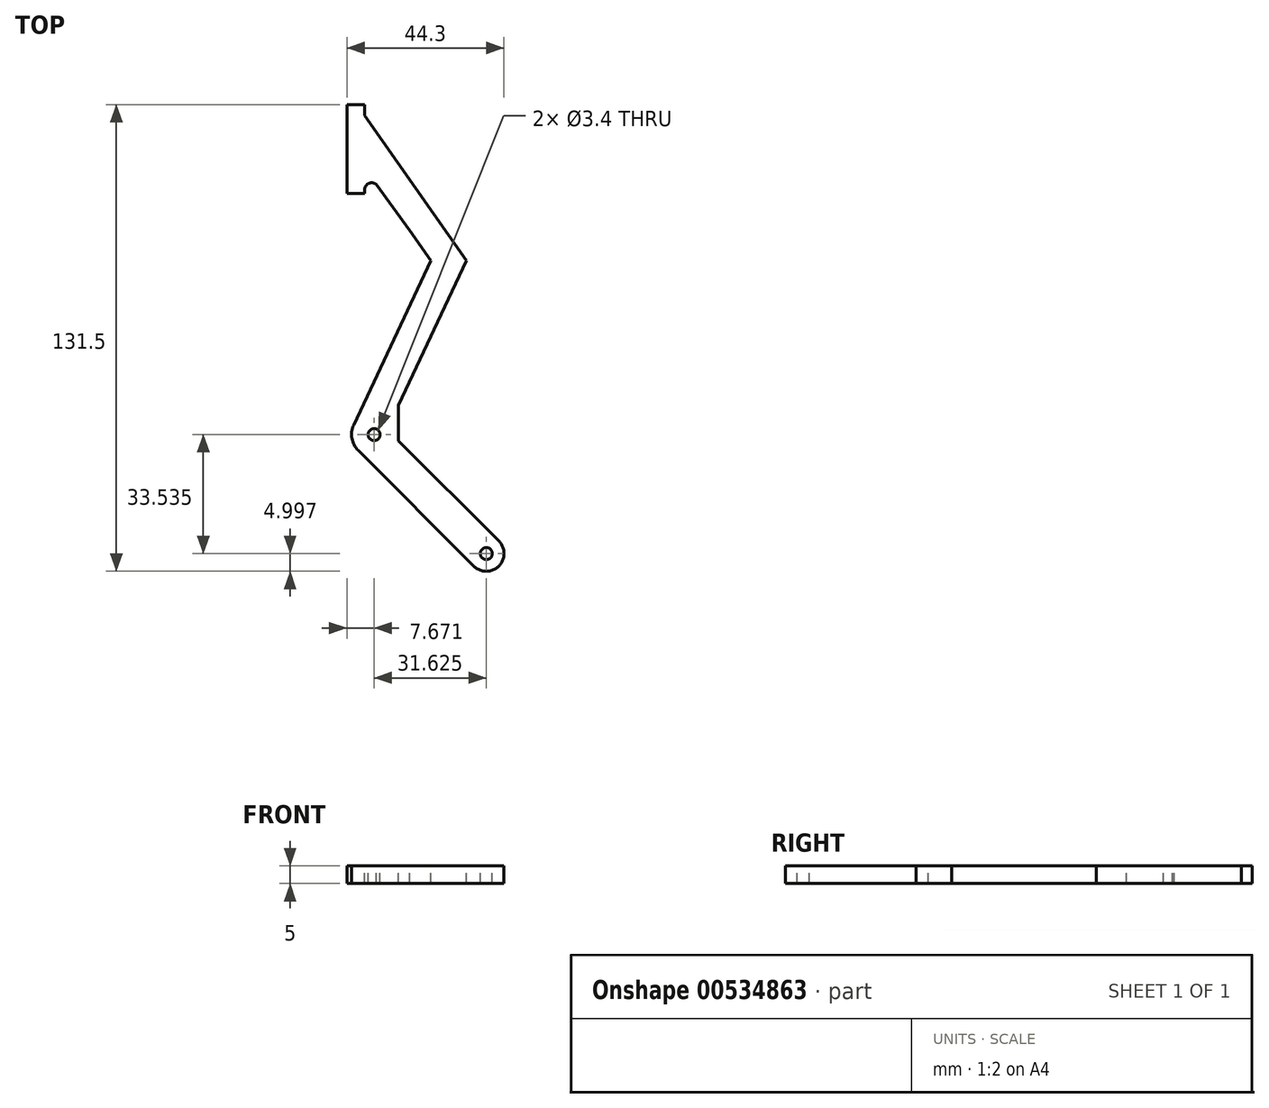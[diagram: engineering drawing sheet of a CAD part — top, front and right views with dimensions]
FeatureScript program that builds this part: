
annotation { "Feature Type Name" : "Feature", "Feature Type Description" : "" }
export const myFeature = defineFeature(function(context is Context, id is Id, definition is map)
    precondition{}
    {
        {
            var Q0;
            Q0=qCreatedBy(makeId("Top.planeOp"),FACE);
            var sketch = newSketch(context, id + "F0", { "sketchPlane" : qUnion([Q0])});
            skLineSegment(sketch, "E0", {"start": v(9.55, 67.67) * mm, "end": v(14.55, 67.67) * mm});
            skLineSegment(sketch, "E1", {"start": v(14.55, 67.67) * mm, "end": v(14.55, 42.67) * mm});
            skLineSegment(sketch, "E2", {"start": v(14.55, 42.67) * mm, "end": v(9.55, 42.67) * mm});
            skLineSegment(sketch, "E3", {"start": v(9.55, 67.67) * mm, "end": v(9.55, 64.67) * mm});
            skLineSegment(sketch, "E4", {"start": v(9.55, 42.67) * mm, "end": v(9.55, 43.67) * mm});
            skLineSegment(sketch, "E5", {"start": v(9.55, 64.67) * mm, "end": v(-19.12, 23.72) * mm});
            skLineSegment(sketch, "E6", {"start": v(-19.12, 23.72) * mm, "end": v(0.01, -17.01) * mm});
            skLineSegment(sketch, "E7", {"start": v(-9.12, 23.72) * mm, "end": v(12.63, -22.6) * mm});
            skLineSegment(sketch, "E8", {"start": v(0.01, -17.01) * mm, "end": v(0.01, -27.01) * mm});
            skLineSegment(sketch, "E9", {"start": v(0.01, -27.01) * mm, "end": v(-28.27, -55.3) * mm});
            skLineSegment(sketch, "E10", {"start": v(-9.12, 23.72) * mm, "end": v(-3.12, 32.3) * mm});
            skArc(sketch, "E11", {"start": v(9.55, 43.67) * mm, "mid": v(8.39, 45.5) * mm, "end": v(6.24, 45.19) * mm});
            skLineSegment(sketch, "E12", {"start": v(-3.12, 32.3) * mm, "end": v(6.24, 45.19) * mm});
            skLineSegment(sketch, "E13", {"start": v(0.01, -27.01) * mm, "end": v(7.08, -34.08) * mm});
            skLineSegment(sketch, "E14", {"start": v(7.08, -34.08) * mm, "end": v(11.38, -29.79) * mm});
            skPoint(sketch, "E15.newPointA", {"position": v(16.39, -30.59) * mm});
            skArc(sketch, "E15.filletArc", {"start": v(11.38, -29.79) * mm, "mid": v(13.14, -26.4) * mm, "end": v(12.63, -22.6) * mm});
            skCircle(sketch, "E16", {"center": v(6.89, -25.3) * mm, "radius": 1.7 * mm});
            skLineSegment(sketch, "E17", {"start": v(7.08, -34.08) * mm, "end": v(-21.2, -62.37) * mm});
            skLineSegment(sketch, "E18", {"start": v(-21.2, -62.37) * mm, "end": v(-28.27, -55.3) * mm});
            skArc(sketch, "E19", {"start": v(-28.27, -55.3) * mm, "mid": v(-28.27, -62.37) * mm, "end": v(-21.2, -62.37) * mm});
            skCircle(sketch, "E20", {"center": v(-24.74, -58.83) * mm, "radius": 1.7 * mm});
            skSolve(sketch);
        }
        {
            var Q0;
            Q0=qSketchRegion(id+"F0",true);
            extrude(context, id + "F1", {"entities" : qUnion([Q0]), "depth" : 5 * mm});
        }
        {
            var Q0;
            Q0=makeQuery(id+"F1.opExtrude","SWEPT_BODY",BODY,{"disambiguationData":[OSD([sQuery(id+"F0.wireOp",EDGE,"E0"),sQuery(id+"F0.wireOp",EDGE,"E1"),sQuery(id+"F0.wireOp",EDGE,"E2"),sQuery(id+"F0.wireOp",EDGE,"E3"),sQuery(id+"F0.wireOp",EDGE,"E4"),sQuery(id+"F0.wireOp",EDGE,"E5"),sQuery(id+"F0.wireOp",EDGE,"E6"),sQuery(id+"F0.wireOp",EDGE,"E7"),sQuery(id+"F0.wireOp",EDGE,"E8"),sQuery(id+"F0.wireOp",EDGE,"E9"),sQuery(id+"F0.wireOp",EDGE,"E10"),sQuery(id+"F0.wireOp",EDGE,"E11"),sQuery(id+"F0.wireOp",EDGE,"E12"),sQuery(id+"F0.wireOp",EDGE,"E14"),sQuery(id+"F0.wireOp",EDGE,"E15.filletArc"),sQuery(id+"F0.wireOp",EDGE,"E16"),sQuery(id+"F0.wireOp",EDGE,"E17"),sQuery(id+"F0.wireOp",EDGE,"E19"),sQuery(id+"F0.wireOp",EDGE,"E20")])]});
            var Q1;
            Q1=makeQuery(id+"F1.opExtrude","CAP_EDGE",EDGE,{"disambiguationData":[OSD([sQuery(id+"F0.wireOp",EDGE,"E1")])],"isStart":false});
            transform(context, id + "F2", {"entities" : qUnion([Q0]), "transformType" : TransformType.ROTATION, "transformAxis" : qUnion([Q1]), "angle" : 180 * degree, "makeCopy" : false});
        }
        {
            var Q0;
            Q0=makeQuery(id+"F1.opExtrude","SWEPT_BODY",BODY,{"disambiguationData":[OSD([sQuery(id+"F0.wireOp",EDGE,"E0"),sQuery(id+"F0.wireOp",EDGE,"E1"),sQuery(id+"F0.wireOp",EDGE,"E2"),sQuery(id+"F0.wireOp",EDGE,"E3"),sQuery(id+"F0.wireOp",EDGE,"E4"),sQuery(id+"F0.wireOp",EDGE,"E5"),sQuery(id+"F0.wireOp",EDGE,"E6"),sQuery(id+"F0.wireOp",EDGE,"E7"),sQuery(id+"F0.wireOp",EDGE,"E8"),sQuery(id+"F0.wireOp",EDGE,"E9"),sQuery(id+"F0.wireOp",EDGE,"E10"),sQuery(id+"F0.wireOp",EDGE,"E11"),sQuery(id+"F0.wireOp",EDGE,"E12"),sQuery(id+"F0.wireOp",EDGE,"E14"),sQuery(id+"F0.wireOp",EDGE,"E15.filletArc"),sQuery(id+"F0.wireOp",EDGE,"E16"),sQuery(id+"F0.wireOp",EDGE,"E17"),sQuery(id+"F0.wireOp",EDGE,"E19"),sQuery(id+"F0.wireOp",EDGE,"E20")])]});
            transform(context, id + "F3", {"entities" : qUnion([Q0]), "transformType" : TransformType.TRANSLATION_3D, "dx" : 7.62 * mm, "dy" : 0 * mm, "dz" : 0 * mm, "makeCopy" : false});
        }
    });
